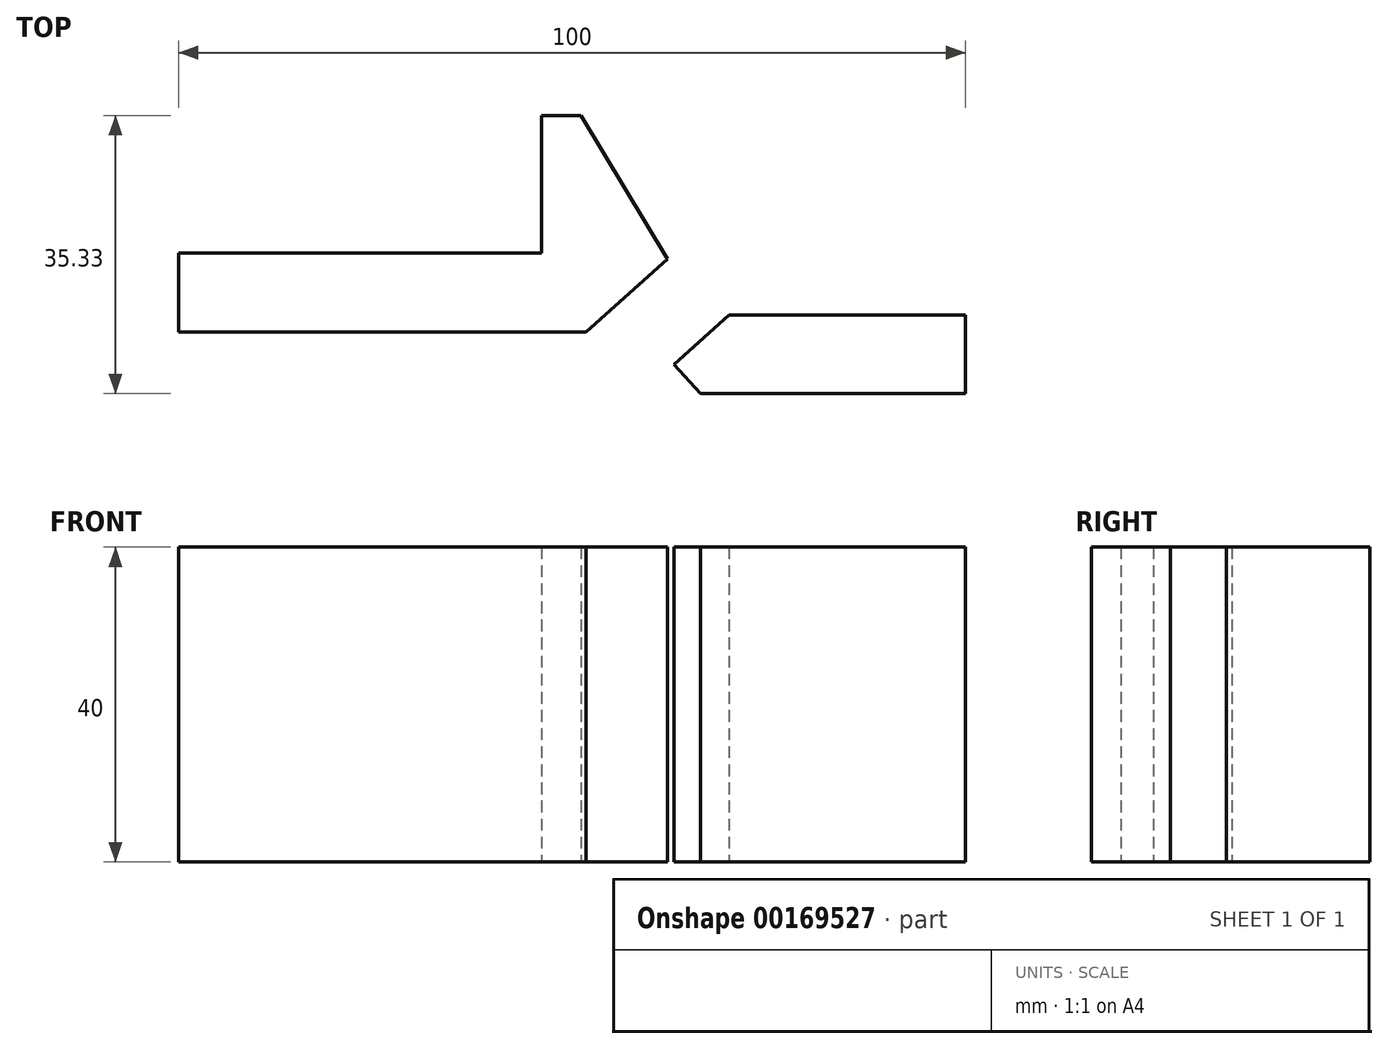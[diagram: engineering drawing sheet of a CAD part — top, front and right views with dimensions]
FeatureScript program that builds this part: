
annotation { "Feature Type Name" : "Feature", "Feature Type Description" : "" }
export const myFeature = defineFeature(function(context is Context, id is Id, definition is map)
    precondition{}
    {
        {
            var Q0;
            Q0=qCreatedBy(makeId("Top.planeOp"),FACE);
            var sketch = newSketch(context, id + "F0", { "sketchPlane" : qUnion([Q0])});
            skLineSegment(sketch, "E0", {"start": v(-24.3, 5) * mm, "end": v(-24.3, -5) * mm});
            skLineSegment(sketch, "E1", {"start": v(-24.3, -5) * mm, "end": v(27.47, -5) * mm});
            skLineSegment(sketch, "E2", {"start": v(27.47, -5) * mm, "end": v(37.81, 4.28) * mm});
            skLineSegment(sketch, "E3", {"start": v(37.81, 4.28) * mm, "end": v(26.83, 22.5) * mm});
            skLineSegment(sketch, "E4", {"start": v(26.83, 22.5) * mm, "end": v(21.83, 22.5) * mm});
            skLineSegment(sketch, "E5", {"start": v(21.83, 22.5) * mm, "end": v(21.83, 5) * mm});
            skLineSegment(sketch, "E6", {"start": v(21.83, 5) * mm, "end": v(-24.3, 5) * mm});
            skLineSegment(sketch, "E7", {"start": v(75.7, -2.84) * mm, "end": v(45.65, -2.84) * mm});
            skLineSegment(sketch, "E8", {"start": v(45.65, -2.84) * mm, "end": v(38.66, -9.12) * mm});
            skLineSegment(sketch, "E9", {"start": v(38.66, -9.12) * mm, "end": v(42, -12.84) * mm});
            skLineSegment(sketch, "E10", {"start": v(42, -12.84) * mm, "end": v(75.7, -12.84) * mm});
            skLineSegment(sketch, "E11", {"start": v(75.7, -12.84) * mm, "end": v(75.7, -2.84) * mm});
            skSolve(sketch);
        }
        {
            var Q0;
            Q0 = qSketchRegion(id + "F0", true);
            extrude(context, id + "F1", {"entities" : qUnion([Q0]), "depth" : 40 * mm});
        }
    });
